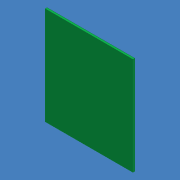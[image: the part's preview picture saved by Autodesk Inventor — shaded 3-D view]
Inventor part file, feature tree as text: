
AUTODESK INVENTOR PART (.ipt)
format: ipt  version: unknown  size: 167,936 bytes
history: native  units: mm (DEFAULTED — no unit token found)
features: extrude x1, sketch x1
ambient origin geometry x8: Origin, YZ Plane, XZ Plane, XY Plane, X Axis, Y Axis, Z Axis, Center Point
feature tree (2):
  extrude  "Extrusion1"  Depth=73.66mm
  sketch  "Sketch1"  dims[d0=66.04mm d1=73.66mm d2=1.4224mm d3=0.0mm]
